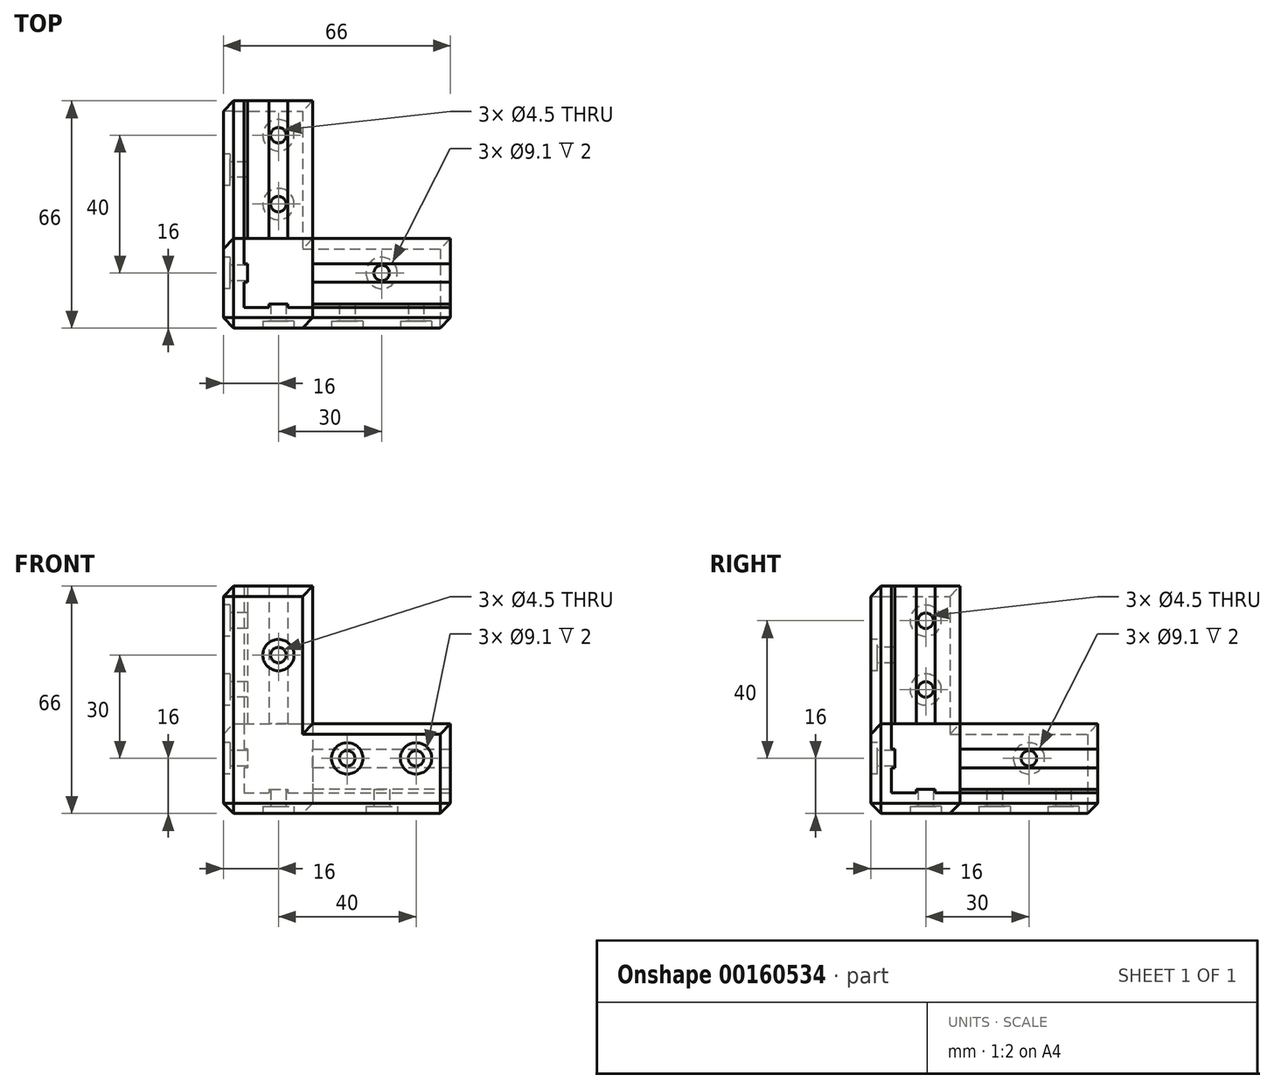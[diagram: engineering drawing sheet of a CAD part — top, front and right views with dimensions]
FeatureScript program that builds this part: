
annotation { "Feature Type Name" : "Feature", "Feature Type Description" : "" }
export const myFeature = defineFeature(function(context is Context, id is Id, definition is map)
    precondition{}
    {
        {
            var Q0;
            Q0=qCreatedBy(makeId("Top.planeOp"),FACE);
            var sketch = newSketch(context, id + "F0", { "sketchPlane" : qUnion([Q0])});
            skLineSegment(sketch, "E0", {"start": v(0, 0) * mm, "end": v(0, 66) * mm});
            skLineSegment(sketch, "E1", {"start": v(0, 66) * mm, "end": v(26, 66) * mm});
            skLineSegment(sketch, "E2", {"start": v(26, 66) * mm, "end": v(26, 26) * mm});
            skLineSegment(sketch, "E3", {"start": v(26, 26) * mm, "end": v(66, 26) * mm});
            skLineSegment(sketch, "E4", {"start": v(66, 26) * mm, "end": v(66, 0) * mm});
            skLineSegment(sketch, "E5", {"start": v(66, 0) * mm, "end": v(0, 0) * mm});
            skLineSegment(sketch, "E6", {"start": v(66, 6) * mm, "end": v(6, 6) * mm, "construction": true});
            skLineSegment(sketch, "E7", {"start": v(6, 6) * mm, "end": v(6, 66) * mm, "construction": true});
            skSolve(sketch);
        }
        {
            var Q0;
            Q0=qSketchRegion(id+"F0",true);
            extrude(context, id + "F1", {"entities" : qUnion([Q0]), "depth" : 6 * mm});
        }
        {
            var Q0;
            Q0=makeQuery(id+"F1.opExtrude","CAP_FACE",FACE,{"disambiguationData":[OSD([sQuery(id+"F0.wireOp",EDGE,"E0"),sQuery(id+"F0.wireOp",EDGE,"E1"),sQuery(id+"F0.wireOp",EDGE,"E2"),sQuery(id+"F0.wireOp",EDGE,"E3"),sQuery(id+"F0.wireOp",EDGE,"E4"),sQuery(id+"F0.wireOp",EDGE,"E5")])],"isStart":false});
            var sketch = newSketch(context, id + "F2", { "sketchPlane" : qUnion([Q0])});
            skLineSegment(sketch, "E8", {"start": v(0, 66) * mm, "end": v(6, 66) * mm});
            skLineSegment(sketch, "E9", {"start": v(6, 66) * mm, "end": v(6, 6) * mm});
            skLineSegment(sketch, "E10", {"start": v(6, 6) * mm, "end": v(66, 6) * mm});
            skLineSegment(sketch, "E11", {"start": v(66, 6) * mm, "end": v(66, 0) * mm});
            skLineSegment(sketch, "E12", {"start": v(66, 0) * mm, "end": v(0, 0) * mm});
            skLineSegment(sketch, "E13", {"start": v(0, 0) * mm, "end": v(0, 66) * mm});
            skSolve(sketch);
        }
        {
            var Q0;
            Q0=makeQuery(id+"F2.imprint","IMPRINT",FACE,{"disambiguationData":[TD([[makeQuery(id+"F2.imprint","IMPRINT",EDGE,{"derivedFrom":sQuery(id+"F2.wireOp",EDGE,"E8")}),-1.0]])]});
            extrude(context, id + "F3", {"entities" : qUnion([Q0]), "operationType" : NewBodyOperationType.ADD, "depth" : 20 * mm});
        }
        {
            var Q0;
            Q0=makeQuery(id+"F3.opExtrude","CAP_FACE",FACE,{"disambiguationData":[OSD([sQuery(id+"F2.wireOp",EDGE,"E8"),sQuery(id+"F2.wireOp",EDGE,"E9"),sQuery(id+"F2.wireOp",EDGE,"E10"),sQuery(id+"F2.wireOp",EDGE,"E11"),sQuery(id+"F2.wireOp",EDGE,"E12"),sQuery(id+"F2.wireOp",EDGE,"E13")])],"isStart":false});
            var sketch = newSketch(context, id + "F4", { "sketchPlane" : qUnion([Q0])});
            skLineSegment(sketch, "E14", {"start": v(6, 26) * mm, "end": v(0, 26) * mm});
            skLineSegment(sketch, "E15", {"start": v(0, 26) * mm, "end": v(0, 0) * mm});
            skLineSegment(sketch, "E16", {"start": v(0, 0) * mm, "end": v(26, 0) * mm});
            skLineSegment(sketch, "E17", {"start": v(26, 0) * mm, "end": v(26, 6) * mm});
            skLineSegment(sketch, "E18", {"start": v(26, 6) * mm, "end": v(6, 6) * mm});
            skLineSegment(sketch, "E19", {"start": v(6, 6) * mm, "end": v(6, 26) * mm});
            skSolve(sketch);
        }
        {
            var Q0;
            Q0=qSketchRegion(id+"F4",true);
            extrude(context, id + "F5", {"entities" : qUnion([Q0]), "operationType" : NewBodyOperationType.ADD, "depth" : 40 * mm});
        }
        {
            var Q0;
            Q0=makeQuery(id+"F1.opExtrude","CAP_FACE",FACE,{"disambiguationData":[OSD([sQuery(id+"F0.wireOp",EDGE,"E0"),sQuery(id+"F0.wireOp",EDGE,"E1"),sQuery(id+"F0.wireOp",EDGE,"E2"),sQuery(id+"F0.wireOp",EDGE,"E3"),sQuery(id+"F0.wireOp",EDGE,"E4"),sQuery(id+"F0.wireOp",EDGE,"E5")])],"isStart":false});
            var sketch = newSketch(context, id + "F6", { "sketchPlane" : qUnion([Q0])});
            skLineSegment(sketch, "E20", {"start": v(66, 16) * mm, "end": v(6, 16) * mm, "construction": true});
            skLineSegment(sketch, "E21", {"start": v(16, 66) * mm, "end": v(16, 6) * mm, "construction": true});
            skLineSegment(sketch, "E22", {"start": v(16, 6) * mm, "end": v(18.71, 6) * mm});
            skLineSegment(sketch, "E23", {"start": v(18.71, 6) * mm, "end": v(18.71, 7) * mm});
            skLineSegment(sketch, "E24", {"start": v(18.71, 7) * mm, "end": v(13.3, 7) * mm});
            skLineSegment(sketch, "E25", {"start": v(13.3, 7) * mm, "end": v(13.3, 6) * mm});
            skLineSegment(sketch, "E26", {"start": v(13.3, 6) * mm, "end": v(16, 6) * mm});
            skLineSegment(sketch, "E27", {"start": v(6, 16) * mm, "end": v(6, 18.7) * mm});
            skLineSegment(sketch, "E28", {"start": v(6, 18.7) * mm, "end": v(7, 18.7) * mm});
            skLineSegment(sketch, "E29", {"start": v(7, 18.7) * mm, "end": v(7, 13.29) * mm});
            skLineSegment(sketch, "E30", {"start": v(7, 13.29) * mm, "end": v(6, 13.29) * mm});
            skLineSegment(sketch, "E31", {"start": v(6, 13.29) * mm, "end": v(6, 16) * mm});
            skSolve(sketch);
        }
        {
            var Q0;
            Q0=qSketchRegion(id+"F6",true);
            extrude(context, id + "F7", {"entities" : qUnion([Q0]), "operationType" : NewBodyOperationType.ADD, "depth" : 60 * mm});
        }
        {
            var Q0;
            Q0=makeQuery(id+"F1.opExtrude","CAP_FACE",FACE,{"disambiguationData":[OSD([sQuery(id+"F0.wireOp",EDGE,"E0"),sQuery(id+"F0.wireOp",EDGE,"E1"),sQuery(id+"F0.wireOp",EDGE,"E2"),sQuery(id+"F0.wireOp",EDGE,"E3"),sQuery(id+"F0.wireOp",EDGE,"E4"),sQuery(id+"F0.wireOp",EDGE,"E5")])],"isStart":false});
            var sketch = newSketch(context, id + "F8", { "sketchPlane" : qUnion([Q0])});
            skLineSegment(sketch, "E32", {"start": v(66, 16) * mm, "end": v(7, 16) * mm, "construction": true});
            skLineSegment(sketch, "E33", {"start": v(66, 16) * mm, "end": v(66, 18.7) * mm});
            skLineSegment(sketch, "E34", {"start": v(66, 18.7) * mm, "end": v(26, 18.7) * mm});
            skLineSegment(sketch, "E35", {"start": v(26, 18.7) * mm, "end": v(26, 13.29) * mm});
            skLineSegment(sketch, "E36", {"start": v(26, 13.29) * mm, "end": v(66, 13.29) * mm});
            skLineSegment(sketch, "E37", {"start": v(66, 13.29) * mm, "end": v(66, 16) * mm});
            skLineSegment(sketch, "E38", {"start": v(16, 66) * mm, "end": v(16, 7) * mm, "construction": true});
            skLineSegment(sketch, "E39", {"start": v(16, 66) * mm, "end": v(13.3, 66) * mm});
            skLineSegment(sketch, "E40", {"start": v(13.3, 66) * mm, "end": v(13.3, 26) * mm});
            skLineSegment(sketch, "E41", {"start": v(13.3, 26) * mm, "end": v(18.7, 26) * mm});
            skLineSegment(sketch, "E42", {"start": v(18.7, 26) * mm, "end": v(18.7, 66) * mm});
            skLineSegment(sketch, "E43", {"start": v(18.7, 66) * mm, "end": v(16, 66) * mm});
            skSolve(sketch);
        }
        {
            var Q0;
            Q0=qSketchRegion(id+"F8",true);
            extrude(context, id + "F9", {"entities" : qUnion([Q0]), "operationType" : NewBodyOperationType.ADD, "flatOperationType" : FlatOperationType.REMOVE, "offsetDistance" : 25 * mm, "depth" : 1 * mm, "domain" : OperationDomain.MODEL});
        }
        {
            var Q0;
            {var subQ1=sQuery(id+"F2.wireOp",EDGE,"E10");var subQ2=sQuery(id+"F0.wireOp",EDGE,"E4");var subQ3=sQuery(id+"F4.wireOp",EDGE,"E18");Q0=makeQuery(id+"F7.boolean.opBoolean","SPLIT",FACE,{"disambiguationData":[TD([makeQuery(id+"F1.opExtrude","SWEPT_FACE",FACE,{"disambiguationData":[OSD([subQ2])]})])],"derivedFrom":makeQuery(id+"F5.boolean.opBoolean","MERGE",FACE,{"derivedFrom":[makeQuery(id+"F3.opExtrude","SWEPT_FACE",FACE,{"disambiguationData":[OSD([subQ1])]}),makeQuery(id+"F5.opExtrude","SWEPT_FACE",FACE,{"disambiguationData":[OSD([subQ3])]})]})});}
            var sketch = newSketch(context, id + "F10", { "sketchPlane" : qUnion([Q0])});
            skLineSegment(sketch, "E44", {"start": v(-66, 16) * mm, "end": v(-26, 16) * mm, "construction": true});
            skLineSegment(sketch, "E45", {"start": v(-66, 16) * mm, "end": v(-66, 13.3) * mm});
            skLineSegment(sketch, "E46", {"start": v(-66, 13.3) * mm, "end": v(-26, 13.3) * mm});
            skLineSegment(sketch, "E47", {"start": v(-26, 13.3) * mm, "end": v(-26, 16) * mm});
            skLineSegment(sketch, "E48", {"start": v(-26, 18.71) * mm, "end": v(-66, 18.71) * mm});
            skLineSegment(sketch, "E49", {"start": v(-66, 18.71) * mm, "end": v(-66, 16) * mm});
            skLineSegment(sketch, "E50", {"start": v(-26, 18.71) * mm, "end": v(-26, 16) * mm});
            skSolve(sketch);
        }
        {
            var Q0;
            Q0=qSketchRegion(id+"F10",true);
            extrude(context, id + "F11", {"entities" : qUnion([Q0]), "operationType" : NewBodyOperationType.ADD, "flatOperationType" : FlatOperationType.REMOVE, "offsetDistance" : 25 * mm, "depth" : 1 * mm, "domain" : OperationDomain.MODEL});
        }
        {
            var Q0;
            {var subQ0=sQuery(id+"F2.wireOp",EDGE,"E9");var subQ3=sQuery(id+"F0.wireOp",EDGE,"E1");var subQ5=sQuery(id+"F4.wireOp",EDGE,"E19");Q0=makeQuery(id+"F7.boolean.opBoolean","SPLIT",FACE,{"disambiguationData":[TD([makeQuery(id+"F1.opExtrude","SWEPT_FACE",FACE,{"disambiguationData":[OSD([subQ3])]})])],"derivedFrom":makeQuery(id+"F5.boolean.opBoolean","MERGE",FACE,{"derivedFrom":[makeQuery(id+"F3.opExtrude","SWEPT_FACE",FACE,{"disambiguationData":[OSD([subQ0])]}),makeQuery(id+"F5.opExtrude","SWEPT_FACE",FACE,{"disambiguationData":[OSD([subQ5])]})]})});}
            var sketch = newSketch(context, id + "F12", { "sketchPlane" : qUnion([Q0])});
            skLineSegment(sketch, "E51", {"start": v(66, 16) * mm, "end": v(26, 16) * mm, "construction": true});
            skLineSegment(sketch, "E52", {"start": v(66, 16) * mm, "end": v(66, 18.71) * mm});
            skLineSegment(sketch, "E53", {"start": v(66, 18.71) * mm, "end": v(26, 18.7) * mm});
            skLineSegment(sketch, "E54", {"start": v(26, 18.7) * mm, "end": v(26, 13.29) * mm});
            skLineSegment(sketch, "E55", {"start": v(26, 13.29) * mm, "end": v(66, 13.29) * mm});
            skLineSegment(sketch, "E56", {"start": v(66, 16) * mm, "end": v(66, 13.29) * mm});
            skSolve(sketch);
        }
        {
            var Q0;
            Q0=qSketchRegion(id+"F12",true);
            extrude(context, id + "F13", {"entities" : qUnion([Q0]), "operationType" : NewBodyOperationType.ADD, "flatOperationType" : FlatOperationType.REMOVE, "offsetDistance" : 25 * mm, "depth" : 1 * mm, "domain" : OperationDomain.MODEL});
        }
        {
            var Q0;
            Q0=makeQuery(id+"F5.boolean.opBoolean","MERGE",FACE,{"derivedFrom":[makeQuery(id+"F3.boolean.opBoolean","MERGE",FACE,{"derivedFrom":[makeQuery(id+"F1.opExtrude","SWEPT_FACE",FACE,{"disambiguationData":[OSD([sQuery(id+"F0.wireOp",EDGE,"E5")])]}),makeQuery(id+"F3.opExtrude","SWEPT_FACE",FACE,{"disambiguationData":[OSD([sQuery(id+"F2.wireOp",EDGE,"E12")])]})]}),makeQuery(id+"F5.opExtrude","SWEPT_FACE",FACE,{"disambiguationData":[OSD([sQuery(id+"F4.wireOp",EDGE,"E16")])]})]});
            var sketch = newSketch(context, id + "F14", { "sketchPlane" : qUnion([Q0])});
            skLineSegment(sketch, "E57", {"start": v(6, 66) * mm, "end": v(6, 6) * mm, "construction": true});
            skLineSegment(sketch, "E58", {"start": v(6, 6) * mm, "end": v(66, 6) * mm, "construction": true});
            skCircle(sketch, "E59", {"center": v(56, 16) * mm, "radius": 2.25 * mm});
            skCircle(sketch, "E60", {"center": v(36, 16) * mm, "radius": 2.25 * mm});
            skCircle(sketch, "E61", {"center": v(16, 46) * mm, "radius": 2.25 * mm});
            skLineSegment(sketch, "E62", {"start": v(26, 26) * mm, "end": v(6, 26) * mm, "construction": true});
            skLineSegment(sketch, "E63", {"start": v(26, 26) * mm, "end": v(26, 6) * mm, "construction": true});
            skSolve(sketch);
        }
        {
            var Q0;
            Q0=makeQuery(id+"F14.imprint","IMPRINT",FACE,{"disambiguationData":[TD([[makeQuery(id+"F14.imprint","IMPRINT",EDGE,{"derivedFrom":sQuery(id+"F14.wireOp",EDGE,"E59")}),1.0]])]});
            var Q1;
            Q1=makeQuery(id+"F14.imprint","IMPRINT",FACE,{"disambiguationData":[TD([[makeQuery(id+"F14.imprint","IMPRINT",EDGE,{"derivedFrom":sQuery(id+"F14.wireOp",EDGE,"E61")}),1.0]])]});
            var Q2;
            Q2=makeQuery(id+"F14.imprint","IMPRINT",FACE,{"disambiguationData":[TD([[makeQuery(id+"F14.imprint","IMPRINT",EDGE,{"derivedFrom":sQuery(id+"F14.wireOp",EDGE,"E60")}),1.0]])]});
            extrude(context, id + "F15", {"entities" : qUnion([Q0, Q1, Q2]), "operationType" : NewBodyOperationType.REMOVE, "endBound" : BoundingType.UP_TO_NEXT, "oppositeDirection" : true, "depth" : 25 * mm});
        }
        {
            var Q0;
            Q0=makeQuery(id+"F5.boolean.opBoolean","MERGE",FACE,{"derivedFrom":[makeQuery(id+"F3.boolean.opBoolean","MERGE",FACE,{"derivedFrom":[makeQuery(id+"F1.opExtrude","SWEPT_FACE",FACE,{"disambiguationData":[OSD([sQuery(id+"F0.wireOp",EDGE,"E0")])]}),makeQuery(id+"F3.opExtrude","SWEPT_FACE",FACE,{"disambiguationData":[OSD([sQuery(id+"F2.wireOp",EDGE,"E13")])]})]}),makeQuery(id+"F5.opExtrude","SWEPT_FACE",FACE,{"disambiguationData":[OSD([sQuery(id+"F4.wireOp",EDGE,"E15")])]})]});
            var sketch = newSketch(context, id + "F16", { "sketchPlane" : qUnion([Q0])});
            skLineSegment(sketch, "E64", {"start": v(-6, 66) * mm, "end": v(-6, 6) * mm, "construction": true});
            skLineSegment(sketch, "E65", {"start": v(-6, 6) * mm, "end": v(-66, 6) * mm, "construction": true});
            skCircle(sketch, "E66", {"center": v(-16, 56) * mm, "radius": 2.25 * mm});
            skCircle(sketch, "E67", {"center": v(-46, 16) * mm, "radius": 2.25 * mm});
            skCircle(sketch, "E68", {"center": v(-16, 36) * mm, "radius": 2.25 * mm});
            skSolve(sketch);
        }
        {
            var Q0;
            Q0=qSketchRegion(id+"F16",true);
            extrude(context, id + "F17", {"entities" : qUnion([Q0]), "operationType" : NewBodyOperationType.REMOVE, "endBound" : BoundingType.UP_TO_NEXT, "oppositeDirection" : true, "depth" : 25 * mm});
        }
        {
            var Q0;
            Q0=makeQuery(id+"F1.opExtrude","CAP_FACE",FACE,{"disambiguationData":[OSD([sQuery(id+"F0.wireOp",EDGE,"E0"),sQuery(id+"F0.wireOp",EDGE,"E1"),sQuery(id+"F0.wireOp",EDGE,"E2"),sQuery(id+"F0.wireOp",EDGE,"E3"),sQuery(id+"F0.wireOp",EDGE,"E4"),sQuery(id+"F0.wireOp",EDGE,"E5")])],"isStart":true});
            var sketch = newSketch(context, id + "F18", { "sketchPlane" : qUnion([Q0])});
            skLineSegment(sketch, "E69", {"start": v(66, -6) * mm, "end": v(6, -6) * mm, "construction": true});
            skLineSegment(sketch, "E70", {"start": v(6, -6) * mm, "end": v(6, -66) * mm, "construction": true});
            skCircle(sketch, "E71", {"center": v(46, -16) * mm, "radius": 2.25 * mm});
            skCircle(sketch, "E72", {"center": v(16, -56) * mm, "radius": 2.25 * mm});
            skCircle(sketch, "E73", {"center": v(16, -36) * mm, "radius": 2.25 * mm});
            skSolve(sketch);
        }
        {
            var Q0;
            Q0=qSketchRegion(id+"F18",true);
            extrude(context, id + "F19", {"entities" : qUnion([Q0]), "operationType" : NewBodyOperationType.REMOVE, "endBound" : BoundingType.UP_TO_NEXT, "oppositeDirection" : true, "depth" : 25 * mm});
        }
        {
            var Q0;
            Q0=makeQuery(id+"F5.boolean.opBoolean","MERGE",FACE,{"derivedFrom":[makeQuery(id+"F3.boolean.opBoolean","MERGE",FACE,{"derivedFrom":[makeQuery(id+"F1.opExtrude","SWEPT_FACE",FACE,{"disambiguationData":[OSD([sQuery(id+"F0.wireOp",EDGE,"E5")])]}),makeQuery(id+"F3.opExtrude","SWEPT_FACE",FACE,{"disambiguationData":[OSD([sQuery(id+"F2.wireOp",EDGE,"E12")])]})]}),makeQuery(id+"F5.opExtrude","SWEPT_FACE",FACE,{"disambiguationData":[OSD([sQuery(id+"F4.wireOp",EDGE,"E16")])]})]});
            var sketch = newSketch(context, id + "F20", { "sketchPlane" : qUnion([Q0])});
            skCircle(sketch, "E74", {"center": v(16, 46) * mm, "radius": 4.55 * mm});
            skCircle(sketch, "E75", {"center": v(36, 16) * mm, "radius": 4.55 * mm});
            skCircle(sketch, "E76", {"center": v(56, 16) * mm, "radius": 4.55 * mm});
            skSolve(sketch);
        }
        {
            var Q0;
            Q0=qSketchRegion(id+"F20",true);
            extrude(context, id + "F21", {"entities" : qUnion([Q0]), "operationType" : NewBodyOperationType.REMOVE, "oppositeDirection" : true, "depth" : 2 * mm});
        }
        {
            var Q0;
            Q0=makeQuery(id+"F5.boolean.opBoolean","MERGE",FACE,{"derivedFrom":[makeQuery(id+"F3.boolean.opBoolean","MERGE",FACE,{"derivedFrom":[makeQuery(id+"F1.opExtrude","SWEPT_FACE",FACE,{"disambiguationData":[OSD([sQuery(id+"F0.wireOp",EDGE,"E0")])]}),makeQuery(id+"F3.opExtrude","SWEPT_FACE",FACE,{"disambiguationData":[OSD([sQuery(id+"F2.wireOp",EDGE,"E13")])]})]}),makeQuery(id+"F5.opExtrude","SWEPT_FACE",FACE,{"disambiguationData":[OSD([sQuery(id+"F4.wireOp",EDGE,"E15")])]})]});
            var sketch = newSketch(context, id + "F22", { "sketchPlane" : qUnion([Q0])});
            skCircle(sketch, "E77", {"center": v(-16, 56) * mm, "radius": 4.55 * mm});
            skCircle(sketch, "E78", {"center": v(-46, 16) * mm, "radius": 4.55 * mm});
            skCircle(sketch, "E79", {"center": v(-16, 36) * mm, "radius": 4.55 * mm});
            skSolve(sketch);
        }
        {
            var Q0;
            Q0=qSketchRegion(id+"F22",true);
            extrude(context, id + "F23", {"entities" : qUnion([Q0]), "operationType" : NewBodyOperationType.REMOVE, "oppositeDirection" : true, "depth" : 2 * mm});
        }
        {
            var Q0;
            Q0=makeQuery(id+"F1.opExtrude","CAP_FACE",FACE,{"disambiguationData":[OSD([sQuery(id+"F0.wireOp",EDGE,"E0"),sQuery(id+"F0.wireOp",EDGE,"E1"),sQuery(id+"F0.wireOp",EDGE,"E2"),sQuery(id+"F0.wireOp",EDGE,"E3"),sQuery(id+"F0.wireOp",EDGE,"E4"),sQuery(id+"F0.wireOp",EDGE,"E5")])],"isStart":true});
            var sketch = newSketch(context, id + "F24", { "sketchPlane" : qUnion([Q0])});
            skCircle(sketch, "E80", {"center": v(16, -56) * mm, "radius": 4.55 * mm});
            skCircle(sketch, "E81", {"center": v(46, -16) * mm, "radius": 4.55 * mm});
            skCircle(sketch, "E82", {"center": v(16, -36) * mm, "radius": 4.55 * mm});
            skSolve(sketch);
        }
        {
            var Q0;
            Q0=qSketchRegion(id+"F24",true);
            extrude(context, id + "F25", {"entities" : qUnion([Q0]), "operationType" : NewBodyOperationType.REMOVE, "oppositeDirection" : true, "depth" : 2 * mm});
        }
        {
            var Q0;
            Q0=makeQuery(id+"F1.opExtrude","CAP_EDGE",EDGE,{"disambiguationData":[OSD([sQuery(id+"F0.wireOp",EDGE,"E5")])],"isStart":true});
            var Q1;
            Q1=makeQuery(id+"F1.opExtrude","CAP_EDGE",EDGE,{"disambiguationData":[OSD([sQuery(id+"F0.wireOp",EDGE,"E0")])],"isStart":true});
            var Q2;
            Q2=makeQuery(id+"F5.boolean.opBoolean","MERGE",EDGE,{"derivedFrom":[makeQuery(id+"F3.boolean.opBoolean","MERGE",EDGE,{"derivedFrom":[makeQuery(id+"F1.opExtrude","SWEPT_EDGE",EDGE,{"disambiguationData":[OSD([sQuery(id+"F0.wireOp",EDGE,"E0"),sQuery(id+"F0.wireOp",EDGE,"E5")])]}),makeQuery(id+"F3.opExtrude","SWEPT_EDGE",EDGE,{"disambiguationData":[OSD([sQuery(id+"F2.wireOp",EDGE,"E12"),sQuery(id+"F2.wireOp",EDGE,"E13")])]})]}),makeQuery(id+"F5.opExtrude","SWEPT_EDGE",EDGE,{"disambiguationData":[OSD([sQuery(id+"F4.wireOp",EDGE,"E15"),sQuery(id+"F4.wireOp",EDGE,"E16")])]})]});
            var Q3;
            Q3=makeQuery(id+"F5.opExtrude","SWEPT_EDGE",EDGE,{"disambiguationData":[OSD([sQuery(id+"F2.wireOp",EDGE,"E13"),sQuery(id+"F4.wireOp",EDGE,"E14"),sQuery(id+"F4.wireOp",EDGE,"E15")])]});
            var Q4;
            Q4=makeQuery(id+"F3.opExtrude","CAP_EDGE",EDGE,{"disambiguationData":[OSD([sQuery(id+"F2.wireOp",EDGE,"E13")])],"isStart":false});
            var Q5;
            Q5=makeQuery(id+"F5.opExtrude","SWEPT_EDGE",EDGE,{"disambiguationData":[OSD([sQuery(id+"F2.wireOp",EDGE,"E12"),sQuery(id+"F4.wireOp",EDGE,"E16"),sQuery(id+"F4.wireOp",EDGE,"E17")])]});
            var Q6;
            Q6=makeQuery(id+"F3.opExtrude","CAP_EDGE",EDGE,{"disambiguationData":[OSD([sQuery(id+"F2.wireOp",EDGE,"E12")])],"isStart":false});
            var Q7;
            Q7=makeQuery(id+"F5.opExtrude","CAP_EDGE",EDGE,{"disambiguationData":[OSD([sQuery(id+"F4.wireOp",EDGE,"E15")])],"isStart":false});
            var Q8;
            Q8=makeQuery(id+"F5.opExtrude","CAP_EDGE",EDGE,{"disambiguationData":[OSD([sQuery(id+"F4.wireOp",EDGE,"E16")])],"isStart":false});
            var Q9;
            Q9=makeQuery(id+"F3.boolean.opBoolean","MERGE",EDGE,{"derivedFrom":[makeQuery(id+"F1.opExtrude","SWEPT_EDGE",EDGE,{"disambiguationData":[OSD([sQuery(id+"F0.wireOp",EDGE,"E0"),sQuery(id+"F0.wireOp",EDGE,"E1")])]}),makeQuery(id+"F3.opExtrude","SWEPT_EDGE",EDGE,{"disambiguationData":[OSD([sQuery(id+"F2.wireOp",EDGE,"E8"),sQuery(id+"F2.wireOp",EDGE,"E13")])]})]});
            var Q10;
            Q10=makeQuery(id+"F1.opExtrude","CAP_EDGE",EDGE,{"disambiguationData":[OSD([sQuery(id+"F0.wireOp",EDGE,"E1")])],"isStart":true});
            var Q11;
            Q11=makeQuery(id+"F3.boolean.opBoolean","MERGE",EDGE,{"derivedFrom":[makeQuery(id+"F1.opExtrude","SWEPT_EDGE",EDGE,{"disambiguationData":[OSD([sQuery(id+"F0.wireOp",EDGE,"E4"),sQuery(id+"F0.wireOp",EDGE,"E5")])]}),makeQuery(id+"F3.opExtrude","SWEPT_EDGE",EDGE,{"disambiguationData":[OSD([sQuery(id+"F2.wireOp",EDGE,"E11"),sQuery(id+"F2.wireOp",EDGE,"E12")])]})]});
            var Q12;
            Q12=makeQuery(id+"F1.opExtrude","CAP_EDGE",EDGE,{"disambiguationData":[OSD([sQuery(id+"F0.wireOp",EDGE,"E4")])],"isStart":true});
            var Q13;
            Q13=makeQuery(id+"F1.opExtrude","CAP_EDGE",EDGE,{"disambiguationData":[OSD([sQuery(id+"F0.wireOp",EDGE,"E3")])],"isStart":true});
            var Q14;
            Q14=makeQuery(id+"F1.opExtrude","CAP_EDGE",EDGE,{"disambiguationData":[OSD([sQuery(id+"F0.wireOp",EDGE,"E2")])],"isStart":true});
            chamfer(context, id + "F26", {"entities" : qUnion([Q0, Q1, Q2, Q3, Q4, Q5, Q6, Q7, Q8, Q9, Q10, Q11, Q12, Q13, Q14]), "width" : 3 * mm, "tangentPropagation" : true});
        }
        {
            var Q0;
            Q0=makeQuery(id+"F1.opExtrude","CAP_FACE",FACE,{"disambiguationData":[OSD([sQuery(id+"F0.wireOp",EDGE,"E0"),sQuery(id+"F0.wireOp",EDGE,"E1"),sQuery(id+"F0.wireOp",EDGE,"E2"),sQuery(id+"F0.wireOp",EDGE,"E3"),sQuery(id+"F0.wireOp",EDGE,"E4"),sQuery(id+"F0.wireOp",EDGE,"E5")])],"isStart":false});
            var sketch = newSketch(context, id + "F27", { "sketchPlane" : qUnion([Q0])});
            skLineSegment(sketch, "E83.bottom", {"start": v(6, 6) * mm, "end": v(26, 6) * mm});
            skLineSegment(sketch, "E83.top", {"start": v(6, 26) * mm, "end": v(26, 26) * mm});
            skLineSegment(sketch, "E83.left", {"start": v(6, 6) * mm, "end": v(6, 26) * mm});
            skLineSegment(sketch, "E83.right", {"start": v(26, 6) * mm, "end": v(26, 26) * mm});
            skSolve(sketch);
        }
        {
            var Q0;
            Q0 = qSketchRegion(id + "F27", true);
            extrude(context, id + "F28", {"entities" : qUnion([Q0]), "operationType" : NewBodyOperationType.ADD, "depth" : 20 * mm});
        }
    });
